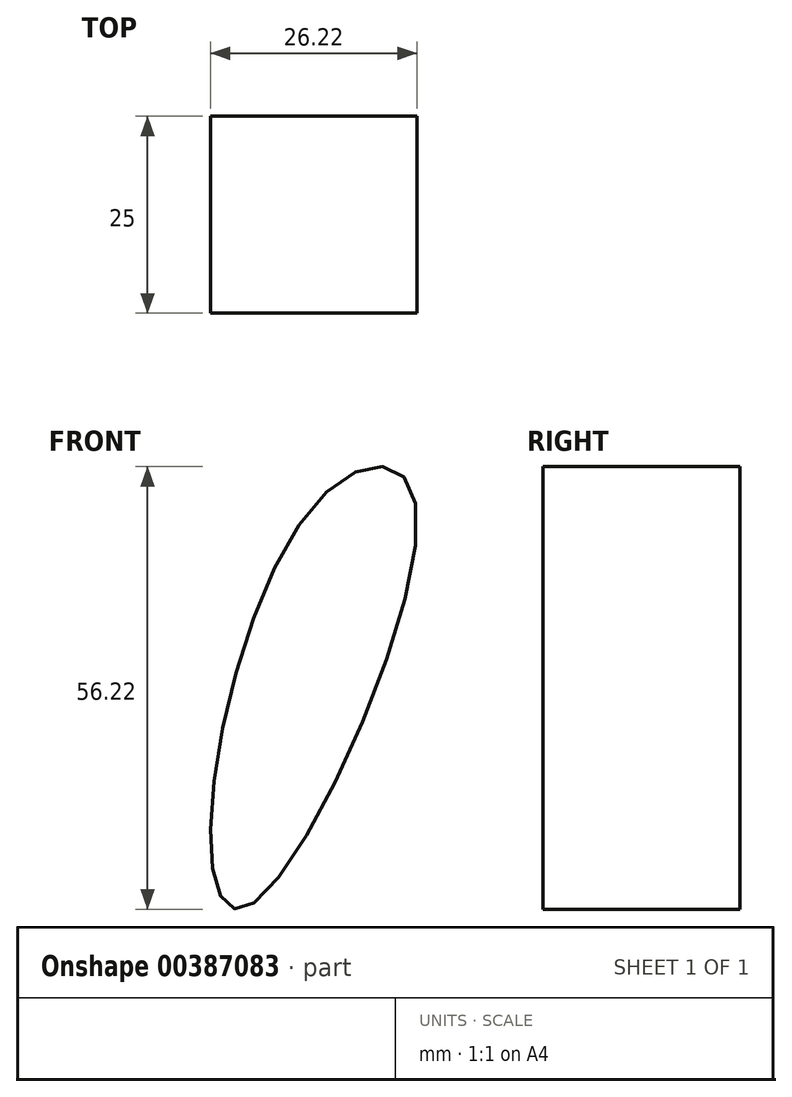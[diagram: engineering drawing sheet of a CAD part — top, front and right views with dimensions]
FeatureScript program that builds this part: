
annotation { "Feature Type Name" : "Feature", "Feature Type Description" : "" }
export const myFeature = defineFeature(function(context is Context, id is Id, definition is map)
    precondition{}
    {
        {
            var Q0;
            Q0=qCreatedBy(makeId("Front.planeOp"),FACE);
            var sketch = newSketch(context, id + "F0", { "sketchPlane" : qUnion([Q0])});
            skFitSpline(sketch, "E0", {"points": [v(-42.45, 43.73) * mm, v(-56.97, -3.59) * mm, v(-52.02, -8.71) * mm, v(-31.35, 43.39) * mm, v(-42.45, 43.73) * mm]});
            skSolve(sketch);
        }
        {
            var Q0;
            Q0 = qSketchRegion(id + "F0", true);
            extrude(context, id + "F1", {"entities" : qUnion([Q0]), "depth" : 25 * mm});
        }
    });
